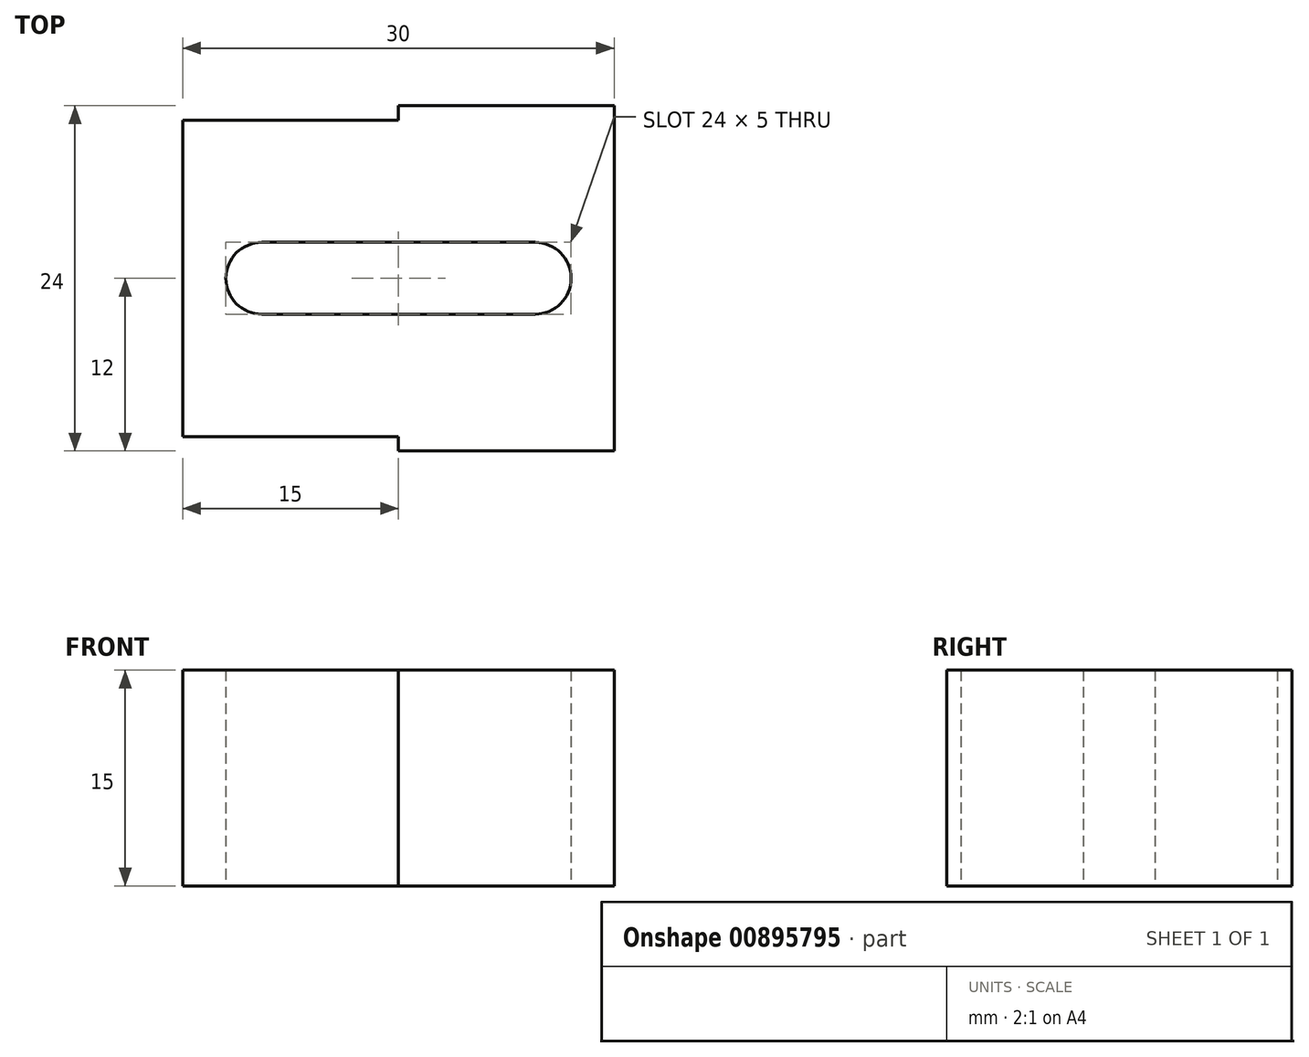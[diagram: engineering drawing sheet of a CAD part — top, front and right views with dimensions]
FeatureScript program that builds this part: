
annotation { "Feature Type Name" : "Feature", "Feature Type Description" : "" }
export const myFeature = defineFeature(function(context is Context, id is Id, definition is map)
    precondition{}
    {
        {
            var Q0;
            Q0=qCreatedBy(makeId("Top.planeOp"),FACE);
            var sketch = newSketch(context, id + "F0", { "sketchPlane" : qUnion([Q0])});
            skLineSegment(sketch, "E0.bottom", {"start": v(-15, 11) * mm, "end": v(0, 11) * mm});
            skLineSegment(sketch, "E0.top", {"start": v(-15, -11) * mm, "end": v(0, -11) * mm});
            skPoint(sketch, "E0.middle", {"position": v(0, 0) * mm});
            skLineSegment(sketch, "E1.bottom", {"start": v(-9.5, 2.5) * mm, "end": v(9.5, 2.5) * mm});
            skLineSegment(sketch, "E1.top", {"start": v(-9.5, -2.5) * mm, "end": v(9.5, -2.5) * mm});
            skLineSegment(sketch, "E1.left", {"start": v(-12, 0) * mm, "end": v(-12, 0) * mm});
            skLineSegment(sketch, "E1.right", {"start": v(12, 0) * mm, "end": v(12, 0) * mm});
            skPoint(sketch, "E2.visualSharp", {"position": v(-12, 2.5) * mm});
            skArc(sketch, "E2.filletArc", {"start": v(-9.5, 2.5) * mm, "mid": v(-11.27, 1.77) * mm, "end": v(-12, 0) * mm});
            skPoint(sketch, "E3.visualSharp", {"position": v(-12, -2.5) * mm});
            skArc(sketch, "E3.filletArc", {"start": v(-12, 0) * mm, "mid": v(-11.27, -1.77) * mm, "end": v(-9.5, -2.5) * mm});
            skPoint(sketch, "E4.visualSharp", {"position": v(12, 2.5) * mm});
            skArc(sketch, "E4.filletArc", {"start": v(12, 0) * mm, "mid": v(11.27, 1.77) * mm, "end": v(9.5, 2.5) * mm});
            skPoint(sketch, "E5.visualSharp", {"position": v(12, -2.5) * mm});
            skArc(sketch, "E5.filletArc", {"start": v(9.5, -2.5) * mm, "mid": v(11.27, -1.77) * mm, "end": v(12, 0) * mm});
            skLineSegment(sketch, "E6", {"start": v(0, 11) * mm, "end": v(0, 12) * mm});
            skLineSegment(sketch, "E7", {"start": v(0, 12) * mm, "end": v(15, 12) * mm});
            skLineSegment(sketch, "E8", {"start": v(15, -12) * mm, "end": v(0, -12) * mm});
            skLineSegment(sketch, "E9", {"start": v(0, -12) * mm, "end": v(0, -11) * mm});
            skLineSegment(sketch, "E10", {"start": v(-15, 11) * mm, "end": v(-15, -11) * mm});
            skLineSegment(sketch, "E11", {"start": v(15, 12) * mm, "end": v(15, -12) * mm});
            skSolve(sketch);
        }
        {
            var Q0;
            Q0=qSketchRegion(id+"F0",true);
            extrude(context, id + "F1", {"entities" : qUnion([Q0]), "depth" : 15 * mm, "offsetDistance" : 25 * mm});
        }
    });
